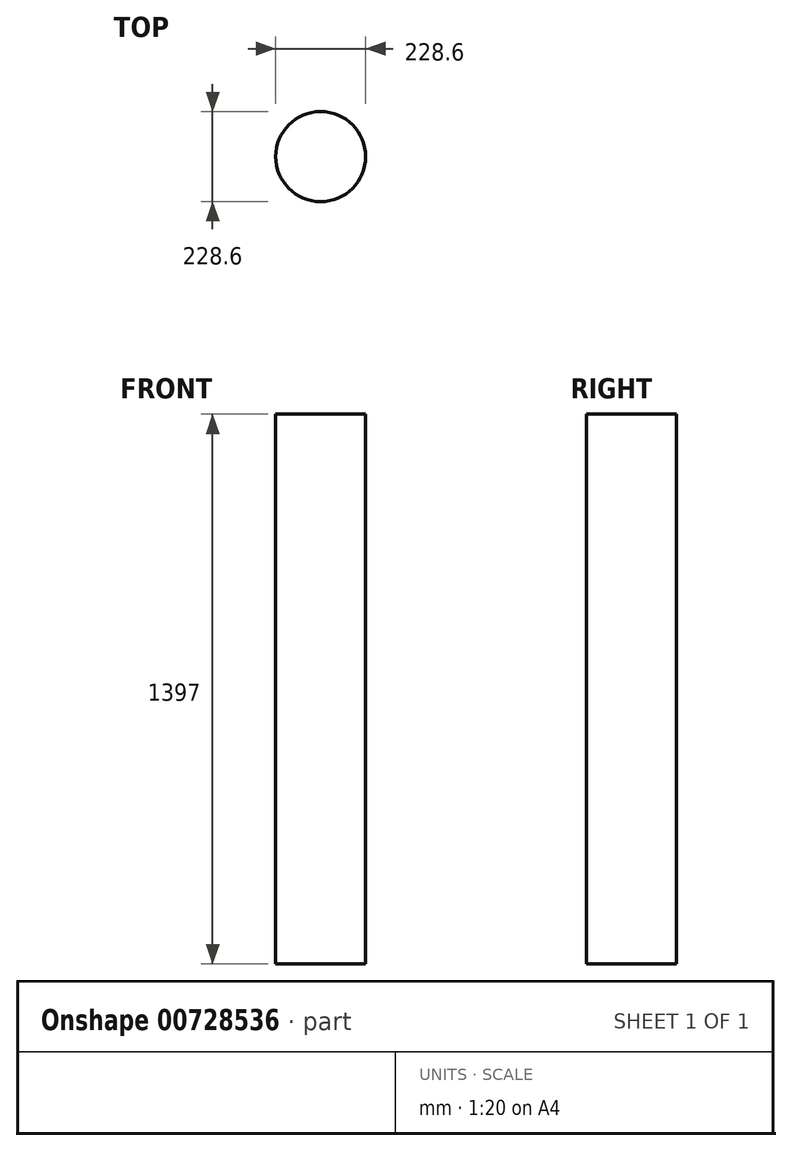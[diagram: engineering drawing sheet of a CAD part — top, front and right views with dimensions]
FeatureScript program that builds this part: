
annotation { "Feature Type Name" : "Feature", "Feature Type Description" : "" }
export const myFeature = defineFeature(function(context is Context, id is Id, definition is map)
    precondition{}
    {
        {
            var Q0;
            Q0=qCreatedBy(makeId("Top.planeOp"),FACE);
            var sketch = newSketch(context, id + "F0", { "sketchPlane" : qUnion([Q0])});
            skCircle(sketch, "E0", {"center": v(0, 0) * mm, "radius": 114.3 * mm});
            skSolve(sketch);
        }
        {
            var Q0;
            Q0 = qSketchRegion(id + "F0", true);
            extrude(context, id + "F1", {"entities" : qUnion([Q0]), "depth" : 1397 * mm, "offsetDistance" : 25.4 * mm});
        }
    });
